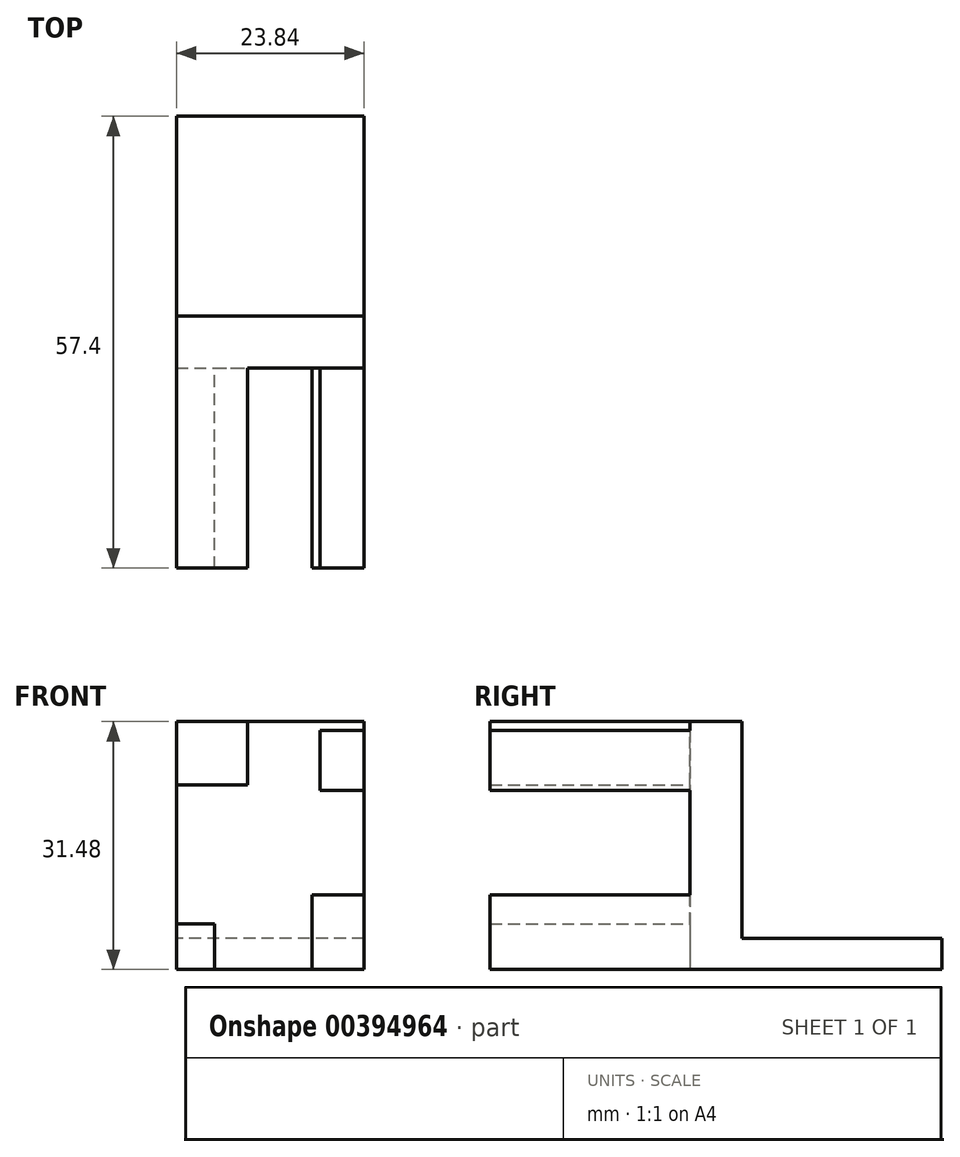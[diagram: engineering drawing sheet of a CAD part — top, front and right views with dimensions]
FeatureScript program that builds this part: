
annotation { "Feature Type Name" : "Feature", "Feature Type Description" : "" }
export const myFeature = defineFeature(function(context is Context, id is Id, definition is map)
    precondition{}
    {
        {
            var Q0;
            Q0=qCreatedBy(makeId("Front.planeOp"),FACE);
            var sketch = newSketch(context, id + "F0", { "sketchPlane" : qUnion([Q0])});
            skLineSegment(sketch, "E0.bottom", {"start": v(0, -1.07) * mm, "end": v(23.84, -1.07) * mm});
            skLineSegment(sketch, "E0.top", {"start": v(0, 30.4) * mm, "end": v(23.84, 30.4) * mm});
            skLineSegment(sketch, "E0.left", {"start": v(0, -1.07) * mm, "end": v(0, 30.4) * mm});
            skLineSegment(sketch, "E0.right", {"start": v(23.84, -1.07) * mm, "end": v(23.84, 30.4) * mm});
            skSolve(sketch);
        }
        {
            var Q0;
            Q0 = qSketchRegion(id + "F0", true);
            extrude(context, id + "F1", {"entities" : qUnion([Q0]), "depth" : 6.6 * mm});
        }
        {
            var Q0;
            Q0=makeQuery(id+"F1.opExtrude","CAP_FACE",FACE,{"disambiguationData":[OSD([sQuery(id+"F0.wireOp",EDGE,"E0.bottom"),sQuery(id+"F0.wireOp",EDGE,"E0.top"),sQuery(id+"F0.wireOp",EDGE,"E0.left"),sQuery(id+"F0.wireOp",EDGE,"E0.right")])],"isStart":false});
            var sketch = newSketch(context, id + "F2", { "sketchPlane" : qUnion([Q0])});
            skLineSegment(sketch, "E1.bottom", {"start": v(0, 22.38) * mm, "end": v(9.07, 22.38) * mm});
            skLineSegment(sketch, "E1.top", {"start": v(0, 30.4) * mm, "end": v(9.07, 30.4) * mm});
            skLineSegment(sketch, "E1.left", {"start": v(0, 22.38) * mm, "end": v(0, 30.4) * mm});
            skLineSegment(sketch, "E1.right", {"start": v(9.07, 22.38) * mm, "end": v(9.07, 30.4) * mm});
            skLineSegment(sketch, "E2.bottom", {"start": v(18.25, 29.28) * mm, "end": v(23.84, 29.28) * mm});
            skLineSegment(sketch, "E2.top", {"start": v(18.25, 21.65) * mm, "end": v(23.84, 21.65) * mm});
            skLineSegment(sketch, "E2.left", {"start": v(18.25, 29.28) * mm, "end": v(18.25, 21.65) * mm});
            skLineSegment(sketch, "E2.right", {"start": v(23.84, 29.28) * mm, "end": v(23.84, 21.65) * mm});
            skLineSegment(sketch, "E3.bottom", {"start": v(0, 4.69) * mm, "end": v(4.85, 4.69) * mm});
            skLineSegment(sketch, "E3.top", {"start": v(0, -1.07) * mm, "end": v(4.85, -1.07) * mm});
            skLineSegment(sketch, "E3.left", {"start": v(0, 4.69) * mm, "end": v(0, -1.07) * mm});
            skLineSegment(sketch, "E3.right", {"start": v(4.85, 4.69) * mm, "end": v(4.85, -1.07) * mm});
            skLineSegment(sketch, "E4.bottom", {"start": v(23.84, 8.37) * mm, "end": v(17.23, 8.37) * mm});
            skLineSegment(sketch, "E4.top", {"start": v(23.84, -1.07) * mm, "end": v(17.23, -1.07) * mm});
            skLineSegment(sketch, "E4.left", {"start": v(23.84, 8.37) * mm, "end": v(23.84, -1.07) * mm});
            skLineSegment(sketch, "E4.right", {"start": v(17.23, 8.37) * mm, "end": v(17.23, -1.07) * mm});
            skSolve(sketch);
        }
        {
            var Q0;
            Q0=makeQuery(id+"F2.imprint","IMPRINT",FACE,{"disambiguationData":[TD([[makeQuery(id+"F2.imprint","IMPRINT",EDGE,{"derivedFrom":sQuery(id+"F2.wireOp",EDGE,"E2.bottom")}),-1.0]])]});
            var Q1;
            Q1=makeQuery(id+"F2.imprint","IMPRINT",FACE,{"disambiguationData":[TD([[makeQuery(id+"F2.imprint","IMPRINT",EDGE,{"derivedFrom":sQuery(id+"F2.wireOp",EDGE,"E3.bottom")}),-1.0]])]});
            var Q2;
            Q2=makeQuery(id+"F2.imprint","IMPRINT",FACE,{"disambiguationData":[TD([[makeQuery(id+"F2.imprint","IMPRINT",EDGE,{"derivedFrom":sQuery(id+"F2.wireOp",EDGE,"E4.bottom")}),1.0]])]});
            var Q3;
            Q3=makeQuery(id+"F2.imprint","IMPRINT",FACE,{"disambiguationData":[TD([[makeQuery(id+"F2.imprint","IMPRINT",EDGE,{"derivedFrom":sQuery(id+"F2.wireOp",EDGE,"E1.bottom")}),1.0]])]});
            extrude(context, id + "F3", {"entities" : qUnion([Q0, Q1, Q2, Q3]), "operationType" : NewBodyOperationType.ADD, "depth" : 25.4 * mm});
        }
        {
            var Q0;
            Q0=makeQuery(id+"F1.opExtrude","CAP_FACE",FACE,{"disambiguationData":[OSD([sQuery(id+"F0.wireOp",EDGE,"E0.bottom"),sQuery(id+"F0.wireOp",EDGE,"E0.top"),sQuery(id+"F0.wireOp",EDGE,"E0.left"),sQuery(id+"F0.wireOp",EDGE,"E0.right")])],"isStart":true});
            var sketch = newSketch(context, id + "F4", { "sketchPlane" : qUnion([Q0])});
            skLineSegment(sketch, "E5.bottom", {"start": v(-23.84, 2.88) * mm, "end": v(0, 2.88) * mm});
            skLineSegment(sketch, "E5.top", {"start": v(-23.84, -1.07) * mm, "end": v(0, -1.07) * mm});
            skLineSegment(sketch, "E5.left", {"start": v(-23.84, 2.88) * mm, "end": v(-23.84, -1.07) * mm});
            skLineSegment(sketch, "E5.right", {"start": v(0, 2.88) * mm, "end": v(0, -1.07) * mm});
            skSolve(sketch);
        }
        {
            var Q0;
            Q0=makeQuery(id+"F4.imprint","IMPRINT",FACE,{"disambiguationData":[TD([[makeQuery(id+"F4.imprint","IMPRINT",EDGE,{"derivedFrom":sQuery(id+"F4.wireOp",EDGE,"E5.bottom")}),-1.0]])]});
            extrude(context, id + "F5", {"entities" : qUnion([Q0]), "operationType" : NewBodyOperationType.ADD, "depth" : 25.4 * mm});
        }
    });
